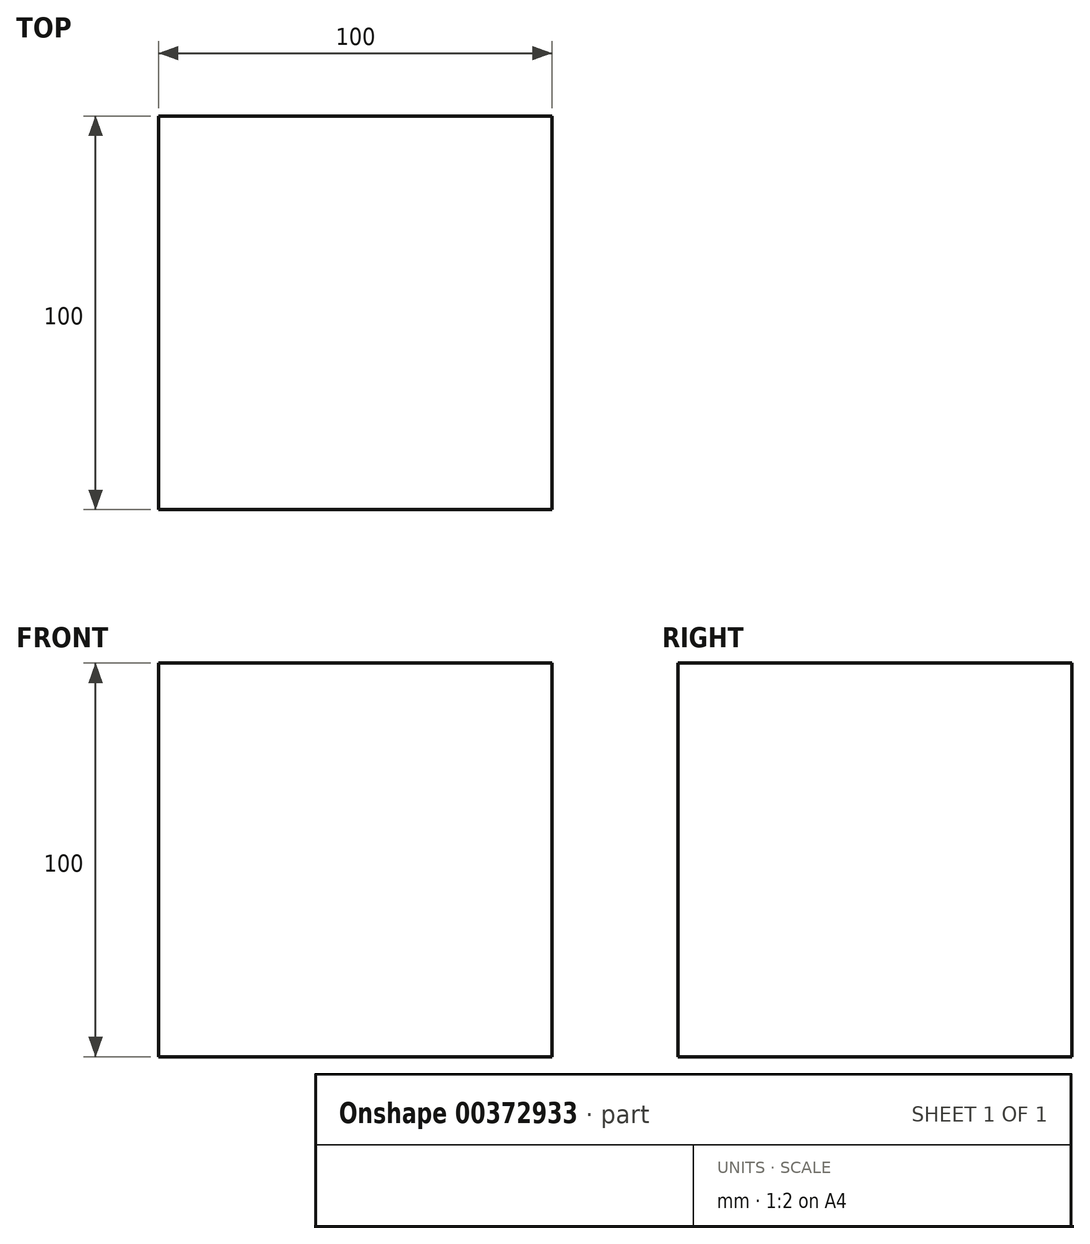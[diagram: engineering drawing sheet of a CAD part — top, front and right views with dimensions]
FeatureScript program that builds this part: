
annotation { "Feature Type Name" : "Feature", "Feature Type Description" : "" }
export const myFeature = defineFeature(function(context is Context, id is Id, definition is map)
    precondition{}
    {
        {
            var Q0;
            Q0=qCreatedBy(makeId("Top.planeOp"),FACE);
            var sketch = newSketch(context, id + "F0", { "sketchPlane" : qUnion([Q0])});
            skLineSegment(sketch, "E0.bottom", {"start": v(-50, 50) * mm, "end": v(50, 50) * mm});
            skLineSegment(sketch, "E0.top", {"start": v(-50, -50) * mm, "end": v(50, -50) * mm});
            skLineSegment(sketch, "E0.left", {"start": v(-50, 50) * mm, "end": v(-50, -50) * mm});
            skLineSegment(sketch, "E0.right", {"start": v(50, 50) * mm, "end": v(50, -50) * mm});
            skPoint(sketch, "E0.middle", {"position": v(0, 0) * mm});
            skSolve(sketch);
        }
        {
            var Q0;
            Q0=makeQuery(id+"F0.imprint","IMPRINT",FACE,{"disambiguationData":[TD([[makeQuery(id+"F0.imprint","IMPRINT",EDGE,{"derivedFrom":sQuery(id+"F0.wireOp",EDGE,"E0.bottom")}),-1.0]])]});
            extrude(context, id + "F1", {"entities" : qUnion([Q0]), "depth" : 100 * mm});
        }
    });
